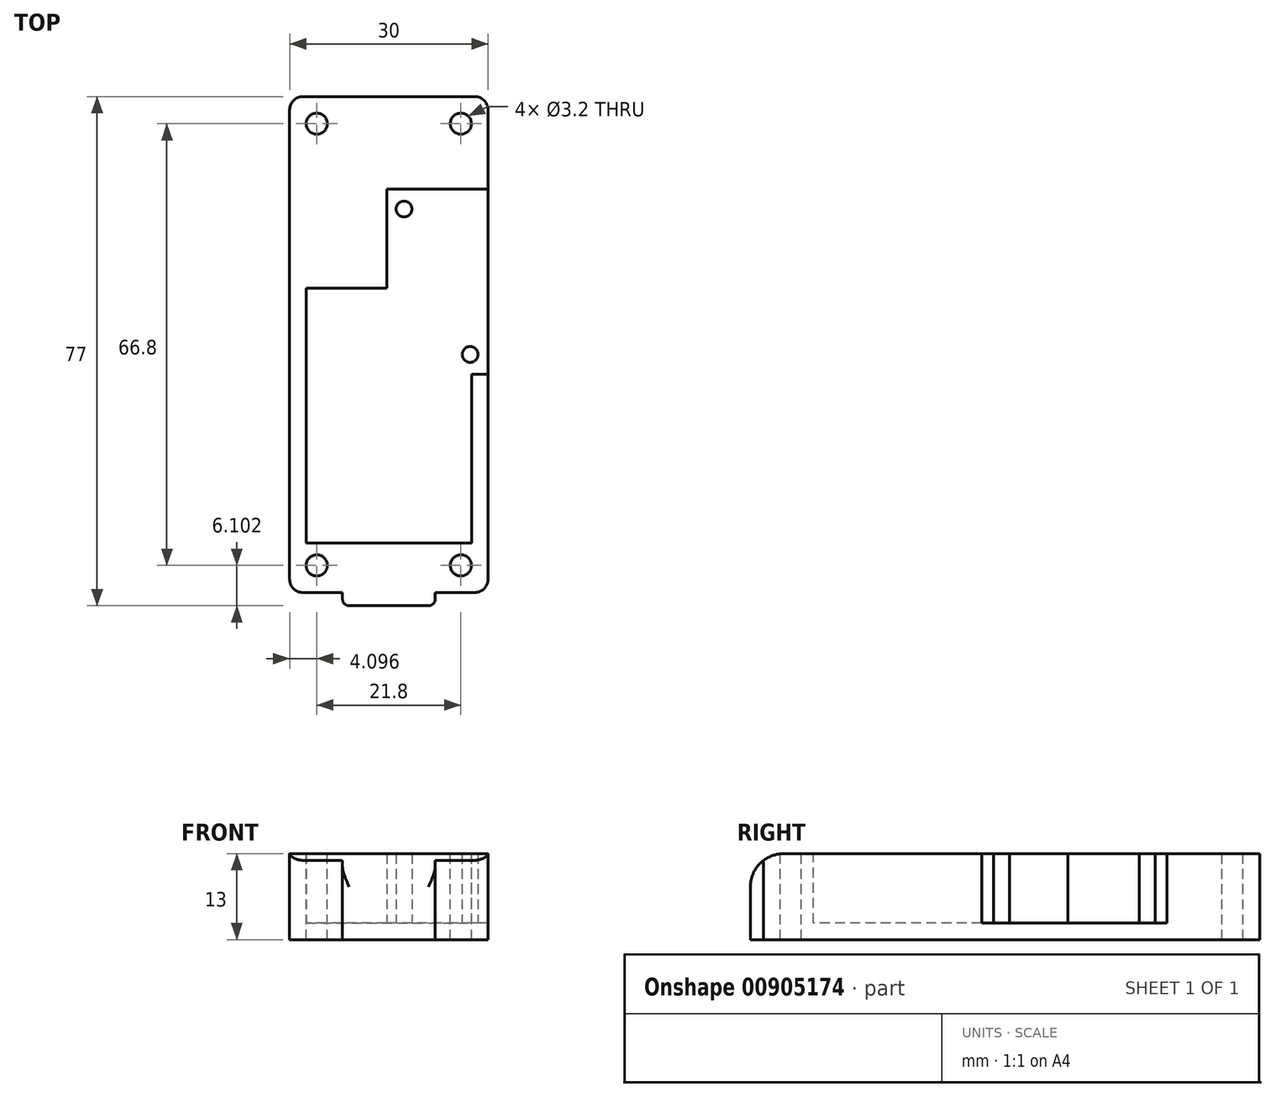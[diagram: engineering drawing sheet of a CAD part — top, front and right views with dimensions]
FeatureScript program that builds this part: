
annotation { "Feature Type Name" : "Feature", "Feature Type Description" : "" }
export const myFeature = defineFeature(function(context is Context, id is Id, definition is map)
    precondition{}
    {
        {
            var Q0;
            Q0=qCreatedBy(makeId("Top.planeOp"),FACE);
            var sketch = newSketch(context, id + "F0", { "sketchPlane" : qUnion([Q0])});
            skLineSegment(sketch, "E0.bottom", {"start": v(-12.9, 28.22) * mm, "end": v(17.1, 28.22) * mm});
            skLineSegment(sketch, "E0.top", {"start": v(-12.9, -26.78) * mm, "end": v(17.1, -26.78) * mm});
            skLineSegment(sketch, "E0.left", {"start": v(-12.9, 28.22) * mm, "end": v(-12.9, -26.78) * mm});
            skLineSegment(sketch, "E0.right", {"start": v(17.1, 28.22) * mm, "end": v(17.1, -26.78) * mm});
            skSolve(sketch);
        }
        {
            var Q0;
            Q0=makeQuery(id+"F0.imprint","IMPRINT",FACE,{"disambiguationData":[TD([[makeQuery(id+"F0.imprint","IMPRINT",EDGE,{"derivedFrom":sQuery(id+"F0.wireOp",EDGE,"E0.bottom")}),-1.0]])]});
            extrude(context, id + "F1", {"entities" : qUnion([Q0]), "depth" : 13 * mm, "offsetDistance" : 25 * mm});
        }
        {
            var Q0;
            Q0=makeQuery(id+"F1.opExtrude","CAP_FACE",FACE,{"disambiguationData":[OSD([sQuery(id+"F0.wireOp",EDGE,"E0.bottom"),sQuery(id+"F0.wireOp",EDGE,"E0.top"),sQuery(id+"F0.wireOp",EDGE,"E0.left"),sQuery(id+"F0.wireOp",EDGE,"E0.right")])],"isStart":false});
            shell(context, id + "F2", {"entities" : qUnion([Q0]), "thickness" : 2.5 * mm});
        }
        {
            var Q0;
            Q0=makeQuery(id+"F1.opExtrude","CAP_FACE",FACE,{"disambiguationData":[OSD([sQuery(id+"F0.wireOp",EDGE,"E0.bottom"),sQuery(id+"F0.wireOp",EDGE,"E0.top"),sQuery(id+"F0.wireOp",EDGE,"E0.left"),sQuery(id+"F0.wireOp",EDGE,"E0.right")])],"isStart":false});
            var sketch = newSketch(context, id + "F3", { "sketchPlane" : qUnion([Q0])});
            skLineSegment(sketch, "E1.bottom", {"start": v(17.1, 24.22) * mm, "end": v(14.6, 24.22) * mm});
            skLineSegment(sketch, "E1.top", {"start": v(17.1, -3.78) * mm, "end": v(14.6, -3.78) * mm});
            skLineSegment(sketch, "E1.left", {"start": v(17.1, 24.22) * mm, "end": v(17.1, -3.78) * mm});
            skLineSegment(sketch, "E1.right", {"start": v(14.6, 24.22) * mm, "end": v(14.6, -3.78) * mm});
            skSolve(sketch);
        }
        {
            var Q0;
            Q0=makeQuery(id+"F3.imprint","IMPRINT",FACE,{"disambiguationData":[TD([[makeQuery(id+"F3.imprint","IMPRINT",EDGE,{"derivedFrom":sQuery(id+"F3.wireOp",EDGE,"E1.bottom")}),1.0]])]});
            var Q1;
            Q1 = qSketchRegion(id + "F5", true);
            extrude(context, id + "F4", {"entities" : qUnion([Q0, Q1]), "operationType" : NewBodyOperationType.REMOVE, "oppositeDirection" : true, "depth" : 10.5 * mm, "offsetDistance" : 25 * mm});
        }
        {
            var Q0;
            Q0=makeQuery(id+"F0.imprint","IMPRINT",FACE,{"disambiguationData":[TD([[makeQuery(id+"F0.imprint","IMPRINT",EDGE,{"derivedFrom":sQuery(id+"F0.wireOp",EDGE,"E0.bottom")}),-1.0]])]});
            var sketch = newSketch(context, id + "F5", { "sketchPlane" : qUnion([Q0])});
            skLineSegment(sketch, "E2.bottom", {"start": v(-10.4, 25.74) * mm, "end": v(1.8, 25.74) * mm});
            skLineSegment(sketch, "E2.top", {"start": v(-10.4, 9.24) * mm, "end": v(1.8, 9.24) * mm});
            skLineSegment(sketch, "E2.left", {"start": v(-10.4, 25.74) * mm, "end": v(-10.4, 9.24) * mm});
            skLineSegment(sketch, "E2.right", {"start": v(1.8, 25.74) * mm, "end": v(1.8, 9.24) * mm});
            skCircle(sketch, "E3", {"center": v(4.4, 21.22) * mm, "radius": 1.2 * mm});
            skCircle(sketch, "E4", {"center": v(14.4, -0.78) * mm, "radius": 1.2 * mm});
            skPoint(sketch, "E5.perimeterSnap0", {"position": v(-10.4, 17.49) * mm});
            skPoint(sketch, "E5.perimeterSnap1", {"position": v(-4.3, 9.24) * mm});
            skLineSegment(sketch, "E6.bottom", {"start": v(1.8, 25.74) * mm, "end": v(14.6, 25.74) * mm});
            skLineSegment(sketch, "E6.top", {"start": v(1.8, 24.22) * mm, "end": v(14.6, 24.22) * mm});
            skLineSegment(sketch, "E6.left", {"start": v(1.8, 25.74) * mm, "end": v(1.8, 24.22) * mm});
            skLineSegment(sketch, "E6.right", {"start": v(14.6, 25.74) * mm, "end": v(14.6, 24.22) * mm});
            skSolve(sketch);
        }
        {
            var Q0;
            Q0=makeQuery(id+"F1.opExtrude","SWEPT_FACE",FACE,{"disambiguationData":[OSD([sQuery(id+"F0.wireOp",EDGE,"E0.bottom")])]});
            var sketch = newSketch(context, id + "F6", { "sketchPlane" : qUnion([Q0])});
            skSolve(sketch);
        }
        {
            var Q0;
            {var subQ0=sQuery(id+"F0.wireOp",EDGE,"E0.bottom");Q0=makeQuery(id+"F6.imprint","IMPRINT",FACE,{"disambiguationData":[TD([[makeQuery(id+"F6.imprint","IMPRINT",EDGE,{"derivedFrom":makeQuery(id+"F1.opExtrude","CAP_EDGE",EDGE,{"disambiguationData":[OSD([subQ0])],"isStart":true})}),-1.0]])]});}
            var Q1;
            Q1 = qSketchRegion(id + "F6", true);
            extrude(context, id + "F7", {"entities" : qUnion([Q0, Q1]), "operationType" : NewBodyOperationType.ADD, "depth" : 10 * mm, "offsetDistance" : 25 * mm});
        }
        {
            var Q0;
            {var subQ0=sQuery(id+"F0.wireOp",EDGE,"E0.bottom");var subQ1=sQuery(id+"F0.wireOp",EDGE,"E0.left");var subQ2=sQuery(id+"F0.wireOp",EDGE,"E0.top");var subQ3=sQuery(id+"F0.wireOp",EDGE,"E0.right");Q0=makeQuery(id+"F7.boolean.opBoolean","MERGE",FACE,{"derivedFrom":[makeQuery(id+"Fi9slC42SYSj50V_1.boolean.opBoolean","MERGE",FACE,{"derivedFrom":[makeQuery(id+"F9mCDE5nnP0mwCd_1.boolean.opBoolean","SPLIT",FACE,{"disambiguationData":[TD([makeQuery(id+"F1.opExtrude","SWEPT_FACE",FACE,{"disambiguationData":[OSD([subQ0])]})])],"derivedFrom":makeQuery(id+"F1.opExtrude","CAP_FACE",FACE,{"disambiguationData":[OSD([subQ0,subQ2,subQ1,subQ3])],"isStart":false})}),makeQuery(id+"Fi9slC42SYSj50V_1.opExtrude","CAP_FACE",FACE,{"disambiguationData":[OSD([sQuery(id+"F5.wireOp",EDGE,"E2.bottom"),sQuery(id+"F5.wireOp",EDGE,"E2.top"),sQuery(id+"F5.wireOp",EDGE,"E2.left"),sQuery(id+"F5.wireOp",EDGE,"E2.right"),sQuery(id+"F5.wireOp",EDGE,"E6.bottom"),sQuery(id+"F5.wireOp",EDGE,"E6.top"),sQuery(id+"F5.wireOp",EDGE,"E6.right")])],"isStart":false})]}),makeQuery(id+"F7.opExtrude","SWEPT_FACE",FACE,{"disambiguationData":[OSD([subQ0]),TDD([makeQuery(id+"F6.imprint","IMPRINT",EDGE,{"derivedFrom":makeQuery(id+"F1.opExtrude","CAP_EDGE",EDGE,{"disambiguationData":[OSD([subQ0])],"isStart":false})})])]})]});}
            var Q1;
            {var subQ0=sQuery(id+"F0.wireOp",EDGE,"E0.bottom");var subQ1=sQuery(id+"F0.wireOp",EDGE,"E0.left");var subQ2=sQuery(id+"F0.wireOp",EDGE,"E0.top");var subQ3=sQuery(id+"F0.wireOp",EDGE,"E0.right");Q1=makeQuery(id+"F7.boolean.opBoolean","MERGE",FACE,{"derivedFrom":[makeQuery(id+"Fi9slC42SYSj50V_1.boolean.opBoolean","MERGE",FACE,{"derivedFrom":[makeQuery(id+"F9mCDE5nnP0mwCd_1.boolean.opBoolean","SPLIT",FACE,{"disambiguationData":[TD([makeQuery(id+"F1.opExtrude","SWEPT_FACE",FACE,{"disambiguationData":[OSD([subQ0])]})])],"derivedFrom":makeQuery(id+"F1.opExtrude","CAP_FACE",FACE,{"disambiguationData":[OSD([subQ0,subQ2,subQ1,subQ3])],"isStart":false})}),makeQuery(id+"Fi9slC42SYSj50V_1.opExtrude","CAP_FACE",FACE,{"disambiguationData":[OSD([sQuery(id+"F5.wireOp",EDGE,"E2.bottom"),sQuery(id+"F5.wireOp",EDGE,"E2.top"),sQuery(id+"F5.wireOp",EDGE,"E2.left"),sQuery(id+"F5.wireOp",EDGE,"E2.right"),sQuery(id+"F5.wireOp",EDGE,"E6.bottom"),sQuery(id+"F5.wireOp",EDGE,"E6.top"),sQuery(id+"F5.wireOp",EDGE,"E6.right")])],"isStart":false})]}),makeQuery(id+"F7.opExtrude","SWEPT_FACE",FACE,{"disambiguationData":[OSD([subQ0]),TDD([makeQuery(id+"F6.imprint","IMPRINT",EDGE,{"derivedFrom":makeQuery(id+"F1.opExtrude","CAP_EDGE",EDGE,{"disambiguationData":[OSD([subQ0])],"isStart":false})})])]})]});}
            var Q2;
            Q2=makeQuery(id+"F7.opExtrude","CAP_FACE",FACE,{"disambiguationData":[OSD([sQuery(id+"F0.wireOp",EDGE,"E0.bottom"),sQuery(id+"F0.wireOp",EDGE,"E0.left"),sQuery(id+"F0.wireOp",EDGE,"E0.right")])],"isStart":false});
            var sketch = newSketch(context, id + "F8", { "sketchPlane" : qUnion([Q0, Q1, Q2])});
            skCircle(sketch, "E7", {"center": v(-8.8, 34.12) * mm, "radius": 1.6 * mm});
            skCircle(sketch, "E8", {"center": v(13, 34.12) * mm, "radius": 1.6 * mm});
            skSolve(sketch);
        }
        {
            var Q0;
            Q0=makeQuery(id+"F7.opExtrude","CAP_EDGE",EDGE,{"disambiguationData":[OSD([sQuery(id+"F0.wireOp",EDGE,"E0.bottom"),sQuery(id+"F0.wireOp",EDGE,"E0.right")])],"isStart":false});
            var Q1;
            Q1=makeQuery(id+"F7.opExtrude","CAP_EDGE",EDGE,{"disambiguationData":[OSD([sQuery(id+"F0.wireOp",EDGE,"E0.bottom"),sQuery(id+"F0.wireOp",EDGE,"E0.left")])],"isStart":false});
            fillet(context, id + "F9", {"entities" : qUnion([Q0, Q1]), "radius" : 2 * mm, "tangentPropagation" : true, "allowEdgeOverflow" : false});
        }
        {
            var Q0;
            Q0=makeQuery(id+"F1.opExtrude","SWEPT_FACE",FACE,{"disambiguationData":[OSD([sQuery(id+"F0.wireOp",EDGE,"E0.top")])]});
            extrude(context, id + "F10", {"entities" : qUnion([Q0]), "operationType" : NewBodyOperationType.ADD, "depth" : 10 * mm, "offsetDistance" : 25 * mm});
        }
        {
            var Q0;
            {var subQ0=sQuery(id+"F0.wireOp",EDGE,"E0.top");var subQ1=sQuery(id+"F0.wireOp",EDGE,"E0.bottom");Q0=makeQuery(id+"F10.boolean.opBoolean","MERGE",FACE,{"derivedFrom":[makeQuery(id+"F7.boolean.opBoolean","MERGE",FACE,{"derivedFrom":[makeQuery(id+"F1.opExtrude","CAP_FACE",FACE,{"disambiguationData":[OSD([subQ1,subQ0,sQuery(id+"F0.wireOp",EDGE,"E0.left"),sQuery(id+"F0.wireOp",EDGE,"E0.right")])],"isStart":false}),makeQuery(id+"F7.opExtrude","SWEPT_FACE",FACE,{"disambiguationData":[OSD([subQ1]),TDD([makeQuery(id+"F6.imprint","IMPRINT",EDGE,{"derivedFrom":makeQuery(id+"F1.opExtrude","CAP_EDGE",EDGE,{"disambiguationData":[OSD([subQ1])],"isStart":false})})])]})]}),makeQuery(id+"F10.opExtrude","SWEPT_FACE",FACE,{"disambiguationData":[OSD([subQ0]),TDD([makeQuery(id+"F1.opExtrude","CAP_EDGE",EDGE,{"disambiguationData":[OSD([subQ0])],"isStart":false})])]})]});}
            var sketch = newSketch(context, id + "F11", { "sketchPlane" : qUnion([Q0])});
            skLineSegment(sketch, "E9.bottom", {"start": v(-10.4, -24.28) * mm, "end": v(14.6, -24.28) * mm});
            skLineSegment(sketch, "E9.top", {"start": v(-10.4, -29.28) * mm, "end": v(14.6, -29.28) * mm});
            skLineSegment(sketch, "E9.left", {"start": v(-10.4, -24.28) * mm, "end": v(-10.4, -29.28) * mm});
            skLineSegment(sketch, "E9.right", {"start": v(14.6, -24.28) * mm, "end": v(14.6, -29.28) * mm});
            skCircle(sketch, "E10", {"center": v(13, -32.68) * mm, "radius": 1.6 * mm});
            skLineSegment(sketch, "E11.bottom", {"start": v(-2.9, -29.28) * mm, "end": v(7.1, -29.28) * mm});
            skLineSegment(sketch, "E11.top", {"start": v(-2.9, -36.78) * mm, "end": v(7.1, -36.78) * mm});
            skLineSegment(sketch, "E11.left", {"start": v(-2.9, -29.28) * mm, "end": v(-2.9, -36.78) * mm});
            skLineSegment(sketch, "E11.right", {"start": v(7.1, -29.28) * mm, "end": v(7.1, -36.78) * mm});
            skCircle(sketch, "E12", {"center": v(-8.8, -32.68) * mm, "radius": 1.6 * mm});
            skSolve(sketch);
        }
        {
            var Q0;
            Q0=makeQuery(id+"F11.imprint","IMPRINT",FACE,{"disambiguationData":[TD([[makeQuery(id+"F11.imprint","IMPRINT",EDGE,{"derivedFrom":sQuery(id+"F11.wireOp",EDGE,"E9.bottom")}),-1.0]])]});
            var Q1;
            Q1=makeQuery(id+"F11.imprint","IMPRINT",FACE,{"disambiguationData":[TD([[makeQuery(id+"F11.imprint","IMPRINT",EDGE,{"derivedFrom":sQuery(id+"F11.wireOp",EDGE,"E11.bottom")}),-1.0]])]});
            extrude(context, id + "F12", {"entities" : qUnion([Q0, Q1]), "operationType" : NewBodyOperationType.REMOVE, "oppositeDirection" : true, "depth" : 10.5 * mm, "offsetDistance" : 25 * mm});
        }
        {
            var Q0;
            Q0=makeQuery(id+"F11.imprint","IMPRINT",FACE,{"disambiguationData":[TD([[makeQuery(id+"F11.imprint","IMPRINT",EDGE,{"derivedFrom":sQuery(id+"F11.wireOp",EDGE,"E10")}),1.0]])]});
            var Q1;
            Q1=makeQuery(id+"F11.imprint","IMPRINT",FACE,{"disambiguationData":[TD([[makeQuery(id+"F11.imprint","IMPRINT",EDGE,{"derivedFrom":sQuery(id+"F11.wireOp",EDGE,"E12")}),1.0]])]});
            extrude(context, id + "F13", {"entities" : qUnion([Q0, Q1]), "operationType" : NewBodyOperationType.REMOVE, "oppositeDirection" : true, "depth" : 13.5 * mm, "offsetDistance" : 25 * mm});
        }
        {
            var Q0;
            Q0 = qSketchRegion(id + "F5", true);
            extrude(context, id + "F14", {"entities" : qUnion([Q0]), "operationType" : NewBodyOperationType.ADD, "depth" : 13 * mm, "offsetDistance" : 25 * mm});
        }
        {
            var Q0;
            Q0=makeQuery(id+"F8.imprint","IMPRINT",FACE,{"disambiguationData":[TD([[makeQuery(id+"F8.imprint","IMPRINT",EDGE,{"derivedFrom":sQuery(id+"F8.wireOp",EDGE,"E7")}),1.0]])]});
            var Q1;
            Q1=makeQuery(id+"F8.imprint","IMPRINT",FACE,{"disambiguationData":[TD([[makeQuery(id+"F8.imprint","IMPRINT",EDGE,{"derivedFrom":sQuery(id+"F8.wireOp",EDGE,"E8")}),1.0]])]});
            var Q2;
            Q2=sQuery(id+"F8.wireOp",EDGE,"E7");
            extrude(context, id + "F15", {"entities" : qUnion([Q0, Q1]), "operationType" : NewBodyOperationType.REMOVE, "surfaceEntities" : qUnion([Q2]), "oppositeDirection" : true, "depth" : 13.5 * mm, "offsetDistance" : 25 * mm});
        }
        {
            var Q0;
            Q0=makeQuery(id+"F10.opExtrude","CAP_EDGE",EDGE,{"disambiguationData":[OSD([sQuery(id+"F0.wireOp",EDGE,"E0.top"),sQuery(id+"F0.wireOp",EDGE,"E0.right")])],"isStart":false});
            var Q1;
            Q1=makeQuery(id+"F10.opExtrude","CAP_EDGE",EDGE,{"disambiguationData":[OSD([sQuery(id+"F0.wireOp",EDGE,"E0.top"),sQuery(id+"F0.wireOp",EDGE,"E0.left")])],"isStart":false});
            fillet(context, id + "F16", {"entities" : qUnion([Q0, Q1]), "radius" : 2 * mm, "tangentPropagation" : true, "allowEdgeOverflow" : false});
        }
        {
            var Q0;
            Q0=makeQuery(id+"F10.opExtrude","CAP_FACE",FACE,{"disambiguationData":[OSD([sQuery(id+"F0.wireOp",EDGE,"E0.top")])],"isStart":false});
            var sketch = newSketch(context, id + "F17", { "sketchPlane" : qUnion([Q0])});
            skLineSegment(sketch, "E13", {"start": v(-4.9, 13) * mm, "end": v(-4.9, 0) * mm});
            skLineSegment(sketch, "E14", {"start": v(-4.9, 0) * mm, "end": v(9.1, 0) * mm});
            skLineSegment(sketch, "E15", {"start": v(9.1, 0) * mm, "end": v(9.1, 13) * mm});
            skSolve(sketch);
        }
        {
            var Q0;
            {var subQ17=sQuery(id+"F17.wireOp",EDGE,"E13");Q0=makeQuery(id+"F17.imprint","IMPRINT",FACE,{"disambiguationData":[TD([[makeQuery(id+"F17.imprint","IMPRINT",EDGE,{"derivedFrom":subQ17}),1.0]])]});}
            extrude(context, id + "F18", {"entities" : qUnion([Q0]), "operationType" : NewBodyOperationType.ADD, "depth" : 2 * mm, "offsetDistance" : 25 * mm});
        }
        {
            var Q0;
            Q0=makeQuery(id+"F18.opExtrude","CAP_EDGE",EDGE,{"disambiguationData":[OSD([sQuery(id+"F17.wireOp",EDGE,"E13")])],"isStart":false});
            var Q1;
            Q1=makeQuery(id+"F18.opExtrude","CAP_EDGE",EDGE,{"disambiguationData":[OSD([sQuery(id+"F17.wireOp",EDGE,"E15")])],"isStart":false});
            fillet(context, id + "F19", {"entities" : qUnion([Q0, Q1]), "radius" : 1 * mm, "tangentPropagation" : true, "allowEdgeOverflow" : false});
        }
        {
            var Q0;
            {var subQ0=sQuery(id+"F11.wireOp",EDGE,"E11.top");var subQ1=sQuery(id+"F11.wireOp",EDGE,"E11.left");var subQ2=sQuery(id+"F0.wireOp",EDGE,"E0.top");Q0=makeQuery(id+"F18.boolean.opBoolean","MERGE",EDGE,{"derivedFrom":[makeQuery(id+"F12.boolean.opBoolean","COPY",EDGE,{"derivedFrom":makeQuery(id+"F12.opExtrude","CAP_EDGE",EDGE,{"disambiguationData":[OSD([subQ1])],"isStart":false})}),makeQuery(id+"F18.opExtrude","SWEPT_EDGE",EDGE,{"disambiguationData":[OSD([subQ2,subQ0,subQ1]),TDD([makeQuery(id+"F17.imprint","INTERSECT",VERTEX,{"derivedFrom":[makeQuery(id+"F12.boolean.opBoolean","COPY",EDGE,{"derivedFrom":makeQuery(id+"F12.opExtrude","SWEPT_EDGE",EDGE,{"disambiguationData":[OSD([subQ2,subQ0,subQ1])]})}),makeQuery(id+"F12.boolean.opBoolean","COPY",EDGE,{"derivedFrom":makeQuery(id+"F12.opExtrude","CAP_EDGE",EDGE,{"disambiguationData":[OSD([subQ0])],"isStart":false})})]})])]})]});}
            var Q1;
            {var subQ0=sQuery(id+"F11.wireOp",EDGE,"E11.top");var subQ1=sQuery(id+"F11.wireOp",EDGE,"E11.right");var subQ2=sQuery(id+"F0.wireOp",EDGE,"E0.top");Q1=makeQuery(id+"F18.boolean.opBoolean","MERGE",EDGE,{"derivedFrom":[makeQuery(id+"F12.boolean.opBoolean","COPY",EDGE,{"derivedFrom":makeQuery(id+"F12.opExtrude","CAP_EDGE",EDGE,{"disambiguationData":[OSD([subQ1])],"isStart":false})}),makeQuery(id+"F18.opExtrude","SWEPT_EDGE",EDGE,{"disambiguationData":[OSD([subQ2,subQ0,subQ1]),TDD([makeQuery(id+"F17.imprint","INTERSECT",VERTEX,{"derivedFrom":[makeQuery(id+"F12.boolean.opBoolean","COPY",EDGE,{"derivedFrom":makeQuery(id+"F12.opExtrude","SWEPT_EDGE",EDGE,{"disambiguationData":[OSD([subQ2,subQ0,subQ1])]})}),makeQuery(id+"F12.boolean.opBoolean","COPY",EDGE,{"derivedFrom":makeQuery(id+"F12.opExtrude","CAP_EDGE",EDGE,{"disambiguationData":[OSD([subQ0])],"isStart":false})})]})])]})]});}
            fillet(context, id + "F20", {"entities" : qUnion([Q0, Q1]), "radius" : 5 * mm, "tangentPropagation" : true, "allowEdgeOverflow" : false});
        }
    });
